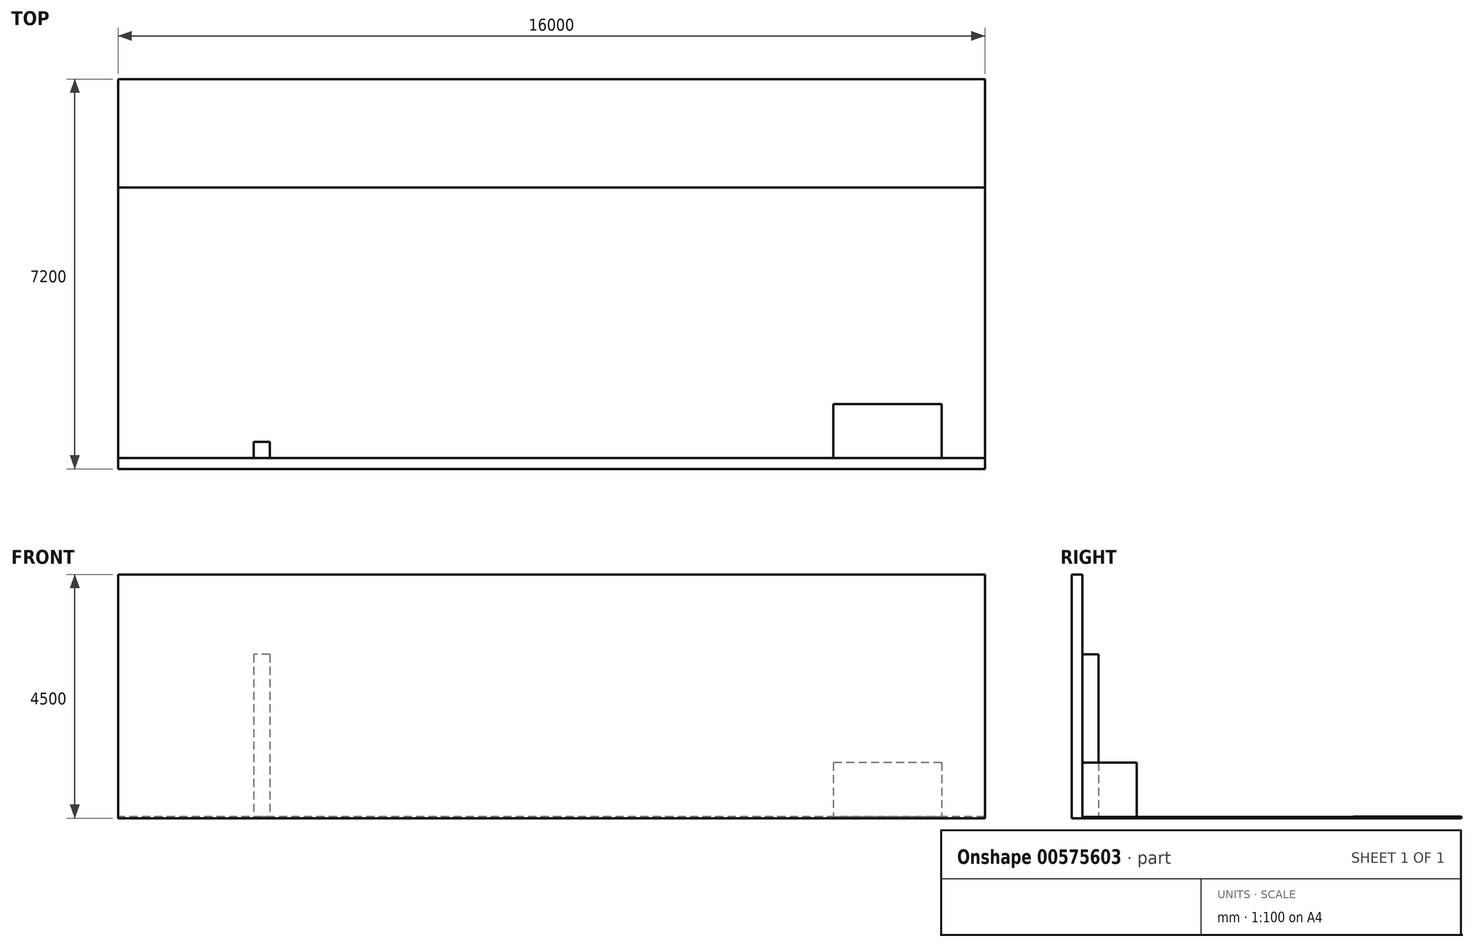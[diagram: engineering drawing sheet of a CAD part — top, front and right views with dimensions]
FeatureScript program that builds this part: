
annotation { "Feature Type Name" : "Feature", "Feature Type Description" : "" }
export const myFeature = defineFeature(function(context is Context, id is Id, definition is map)
    precondition{}
    {
        {
            var Q0;
            Q0=qCreatedBy(makeId("Top.planeOp"),FACE);
            var sketch = newSketch(context, id + "F0", { "sketchPlane" : qUnion([Q0])});
            skLineSegment(sketch, "E0.bottom", {"start": v(8000, -3500) * mm, "end": v(-8000, -3500) * mm});
            skLineSegment(sketch, "E0.top", {"start": v(8000, 3500) * mm, "end": v(-8000, 3500) * mm});
            skLineSegment(sketch, "E0.left", {"start": v(8000, -3500) * mm, "end": v(8000, 3500) * mm});
            skLineSegment(sketch, "E0.right", {"start": v(-8000, -3500) * mm, "end": v(-8000, 3500) * mm});
            skPoint(sketch, "E0.middle", {"position": v(0, 0) * mm});
            skSolve(sketch);
        }
        {
            var Q0;
            Q0 = qSketchRegion(id + "F0", true);
            extrude(context, id + "F1", {"entities" : qUnion([Q0]), "depth" : 25 * mm, "offsetDistance" : 25 * mm});
        }
        {
            var Q0;
            Q0=makeQuery(id+"F1.opExtrude","CAP_FACE",FACE,{"disambiguationData":[OSD([sQuery(id+"F0.wireOp",EDGE,"E0.bottom"),sQuery(id+"F0.wireOp",EDGE,"E0.top"),sQuery(id+"F0.wireOp",EDGE,"E0.left"),sQuery(id+"F0.wireOp",EDGE,"E0.right")])],"isStart":false});
            var sketch = newSketch(context, id + "F2", { "sketchPlane" : qUnion([Q0])});
            skLineSegment(sketch, "E1.bottom", {"start": v(-8000, 3500) * mm, "end": v(8000, 3500) * mm});
            skLineSegment(sketch, "E1.top", {"start": v(-8000, 1500) * mm, "end": v(8000, 1500) * mm});
            skLineSegment(sketch, "E1.left", {"start": v(-8000, 3500) * mm, "end": v(-8000, 1500) * mm});
            skLineSegment(sketch, "E1.right", {"start": v(8000, 3500) * mm, "end": v(8000, 1500) * mm});
            skSolve(sketch);
        }
        {
            var Q0;
            Q0=makeQuery(id+"F1.opExtrude","SWEPT_FACE",FACE,{"disambiguationData":[OSD([sQuery(id+"F0.wireOp",EDGE,"E0.bottom")])]});
            var sketch = newSketch(context, id + "F3", { "sketchPlane" : qUnion([Q0])});
            skLineSegment(sketch, "E2.bottom", {"start": v(-8000, 0) * mm, "end": v(8000, 0) * mm});
            skLineSegment(sketch, "E2.top", {"start": v(-8000, 4500) * mm, "end": v(8000, 4500) * mm});
            skLineSegment(sketch, "E2.left", {"start": v(-8000, 0) * mm, "end": v(-8000, 4500) * mm});
            skLineSegment(sketch, "E2.right", {"start": v(8000, 0) * mm, "end": v(8000, 4500) * mm});
            skSolve(sketch);
        }
        {
            var Q0;
            Q0 = qSketchRegion(id + "F2", true);
            extrude(context, id + "F4", {"entities" : qUnion([Q0]), "operationType" : NewBodyOperationType.ADD, "depth" : 2.5 * mm, "offsetDistance" : 25 * mm});
        }
        {
            var Q0;
            Q0 = qSketchRegion(id + "F3", true);
            extrude(context, id + "F5", {"entities" : qUnion([Q0]), "depth" : 200 * mm, "offsetDistance" : 25 * mm});
        }
        {
            var Q0;
            Q0=makeQuery(id+"F1.opExtrude","CAP_FACE",FACE,{"disambiguationData":[OSD([sQuery(id+"F0.wireOp",EDGE,"E0.bottom"),sQuery(id+"F0.wireOp",EDGE,"E0.top"),sQuery(id+"F0.wireOp",EDGE,"E0.left"),sQuery(id+"F0.wireOp",EDGE,"E0.right")])],"isStart":false});
            var sketch = newSketch(context, id + "F6", { "sketchPlane" : qUnion([Q0])});
            skLineSegment(sketch, "E3.bottom", {"start": v(-5500, -3500) * mm, "end": v(-5200, -3500) * mm});
            skLineSegment(sketch, "E3.top", {"start": v(-5500, -3200) * mm, "end": v(-5200, -3200) * mm});
            skLineSegment(sketch, "E3.left", {"start": v(-5500, -3500) * mm, "end": v(-5500, -3200) * mm});
            skLineSegment(sketch, "E3.right", {"start": v(-5200, -3500) * mm, "end": v(-5200, -3200) * mm});
            skSolve(sketch);
        }
        {
            var Q0;
            Q0 = qSketchRegion(id + "F6", true);
            extrude(context, id + "F7", {"entities" : qUnion([Q0]), "depth" : 3000 * mm, "offsetDistance" : 25 * mm});
        }
        {
            var Q0;
            Q0=makeQuery(id+"F1.opExtrude","CAP_FACE",FACE,{"disambiguationData":[OSD([sQuery(id+"F0.wireOp",EDGE,"E0.bottom"),sQuery(id+"F0.wireOp",EDGE,"E0.top"),sQuery(id+"F0.wireOp",EDGE,"E0.left"),sQuery(id+"F0.wireOp",EDGE,"E0.right")])],"isStart":false});
            var sketch = newSketch(context, id + "F8", { "sketchPlane" : qUnion([Q0])});
            skLineSegment(sketch, "E4.bottom", {"start": v(7200, -3500) * mm, "end": v(5200, -3500) * mm});
            skLineSegment(sketch, "E4.top", {"start": v(7200, -2500) * mm, "end": v(5200, -2500) * mm});
            skLineSegment(sketch, "E4.left", {"start": v(7200, -3500) * mm, "end": v(7200, -2500) * mm});
            skLineSegment(sketch, "E4.right", {"start": v(5200, -3500) * mm, "end": v(5200, -2500) * mm});
            skSolve(sketch);
        }
        {
            var Q0;
            Q0 = qSketchRegion(id + "F8", true);
            extrude(context, id + "F9", {"entities" : qUnion([Q0]), "depth" : 1000 * mm, "offsetDistance" : 25 * mm});
        }
    });
